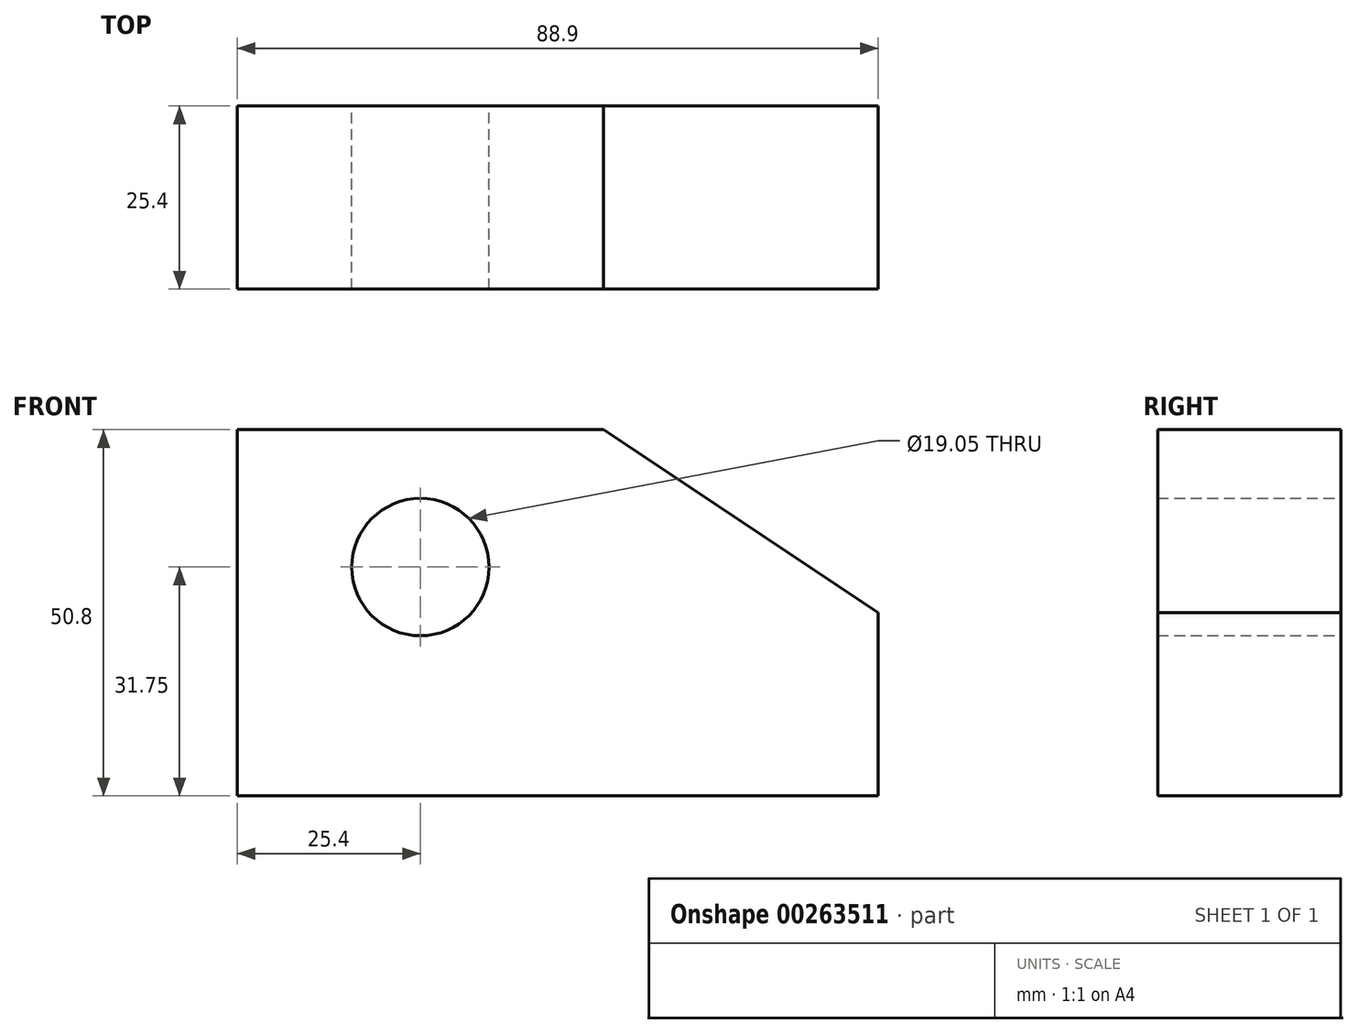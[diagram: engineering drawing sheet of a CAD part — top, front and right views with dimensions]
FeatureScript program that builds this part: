
annotation { "Feature Type Name" : "Feature", "Feature Type Description" : "" }
export const myFeature = defineFeature(function(context is Context, id is Id, definition is map)
    precondition{}
    {
        {
            var Q0;
            Q0=qCreatedBy(makeId("Front.planeOp"),FACE);
            var sketch = newSketch(context, id + "F0", { "sketchPlane" : qUnion([Q0])});
            skLineSegment(sketch, "E0", {"start": v(0, 0) * mm, "end": v(88.9, 0) * mm});
            skLineSegment(sketch, "E1", {"start": v(88.9, 0) * mm, "end": v(88.9, 25.4) * mm});
            skLineSegment(sketch, "E2", {"start": v(88.9, 25.4) * mm, "end": v(50.8, 50.8) * mm});
            skLineSegment(sketch, "E3", {"start": v(50.8, 50.8) * mm, "end": v(0, 50.8) * mm});
            skLineSegment(sketch, "E4", {"start": v(0, 50.8) * mm, "end": v(0, 0) * mm});
            skCircle(sketch, "E5", {"center": v(25.4, 31.75) * mm, "radius": 9.53 * mm});
            skSolve(sketch);
        }
        {
            var Q0;
            Q0=makeQuery(id+"F0.imprint","IMPRINT",FACE,{"disambiguationData":[TD([[makeQuery(id+"F0.imprint","IMPRINT",EDGE,{"derivedFrom":sQuery(id+"F0.wireOp",EDGE,"E0")}),1.0]])]});
            extrude(context, id + "F1", {"entities" : qUnion([Q0]), "depth" : 25.4 * mm, "symmetric" : true});
        }
    });
